# Revit family: Platek_Spring_Floodlight
name_source: partatom
category: Apparecchi per illuminazione
revit_build: Autodesk Revit 2017 (Build: 20160225_1515(x64)
units: mm (PartAtom-declared; Revit-internal decimal feet)

## family parameters
Basato su piano di lavoro = Sì
Condiviso = No
Punto di calcolo locali = No
Quota connettore circolare = Usa diametro
Sempre verticale = No
Sorgente d'illuminazione = No
Taglio con vuoti quando caricato = No
Tipo di parte = Normale

## types (5) — shared parameters
Angolo di inclinazione = 0.00°
Body = PLK_06_Grey
Body Inside = PLK_Optic
CRI = >80
Cable Lenght = 3 m Cable Length
Carico apparente = 0 VA
Colour Temprature = 3000 K
Commenti sul tipo = Facades, Columns, Streets, Trees
Descrizione = Outdoor Lighting, Wall mounted, Ground mounted, Pole mounted
Diffuse Type = Transparent Glass
Dimmable = NO
Energy Efficiency Rating = A/A+/A++
Frequency = 50/60Hz
IK Rating = IK 06
IP Rating = IP 65
Immagine tipo = spring.jpg
Insulation Class = 2
LED Protection = Surge protection included
Light Source = PLK_Light Source
Modello = Spring
Mounting Type = Wall/Pole/Ground
Nota chiave = 5mm flat tempered glass; Other Led Colours available on request
PLATEK Finishes = Painted Aluminium Avalaible in Anthracite/Black/White/Corten/Bronze
Part Body = PLK_Aluminium_Black
Power Supply Unit = Included
Product Dimension = L300 x W200x H262mm
Product Documentation Link = http://www.platek.eu
Product Page URL = http://www.platek.eu
Produttore = PLATEK SRL
Screws = PLK_Full Inox
Supply Voltage = 230 V
Supply Voltage Max = 240 V
Supply Voltage Min = 220 V
URL = www.platek.eu
zero-valued in all types: Prospetto di default

## per-type parameters (varying)
| type | Beam Angle | Codice assieme | Lampada | Luminaire Luminous Flux | Luminaire Wattage | Luminaure Luminous Intensity | Manufacturer Comment | PLATEK Article Code | PLK_Photometrics |
| 8815811_45W_LED_3000K_Transparent Glass | 18.00° | 8815811.08(Anthracite); 8815811.01(Black); 8815811.02(White); 8815811.07(Corten); 8815811.09(Bronze)-Ellipsoidal filter: 8918660; Sandblasted filter: 8918665; Visor Shield: 8905020.01; Tube Shield: 8905090.01; Spike: 9005600 | COB LED | 3910 lm | 45 W | 25700 cd | Spot Optic, free rotation | 8815811 | PLK_Spring_Photometrics : 8815811 |
| 8815813_45W_LED_3000K_Transparent Glass | 38.00° | 8815813.08(Anthracite); 8815813.01(Black); 8815813.02(White); 8815813.07(Corten); 8815813.09(Bronze)-Ellipsoidal filter: 8918660; Sandblasted filter: 8918665; Visor Shield: 8905020.01; Tube Shield: 8905090.01; Spike: 9005600 | COB LED | 4090 lm | 45 W | 6205 cd | Medium Optic, free rotation | 8815813 | PLK_Spring_Photometrics : 8815813 |
| 8422511_44W_LED_3000K_Transparent Glass | 9.00° | 8422511.08(Anthracite); 8422511.01(Black); 8422511.02(White); 8422511.07(Corten); 8422511.09(Bronze)-Ellipsoidal filter: 8918660; Sandblasted filter: 8918665; Visor Shield: 8905020.01; Tube Shield: 8905090.01; Spike: 9005600 | LED | 3675 lm | 44 W | 71406 cd | Spot Optic, free rotation | 8422511 | PLK_Spring_Photometrics : 8422511 |
| 8422513_44W_LED_3000K_Transparent Glass | 28.00° | 8422513.08(Anthracite); 8422513.01(Black); 8422513.02(White); 8422513.07(Corten); 8422513.09(Bronze)-Ellipsoidal filter: 8918660; Sandblasted filter: 8918665; Visor Shield: 8905020.01; Tube Shield: 8905090.01; Spike: 9005600 | LED | 3645 lm | 44 W | 13922 cd | Medium Optic, free rotation | 8422513 | PLK_Spring_Photometrics : 8422513 |
| 8422518_44W_LED_3000K_Transparent Glass | 45.00° | 8422518.08(Anthracite); 8422518.01(Black); 8422518.02(White); 8422518.07(Corten); 8422518.09(Bronze)-Ellipsoidal filter: 8918660; Sandblasted filter: 8918665; Visor Shield: 8905020.01; Tube Shield: 8905090.01; Spike: 9005600 | LED | 3080 lm | 44 W | 4981 cd | Wide Optic, free rotation | 8422518 | PLK_Spring_Photometrics : 8422518 |

## geometry (parser evidence)
native form markers: Sweep x2
no freeform markers — native parametric forms only
